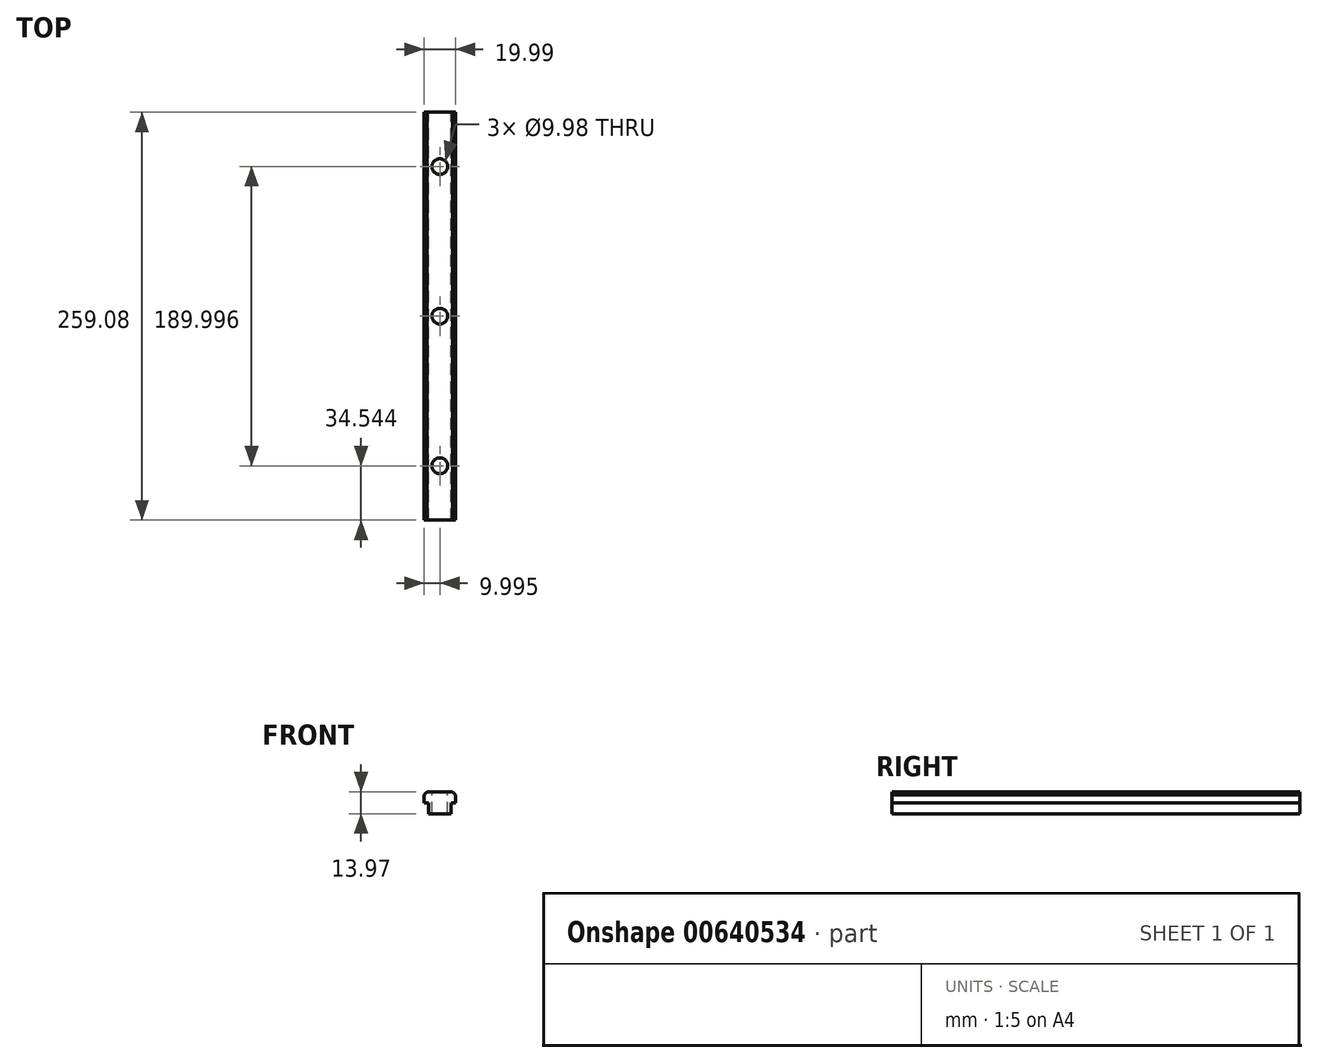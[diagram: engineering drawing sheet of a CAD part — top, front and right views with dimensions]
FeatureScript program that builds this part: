
annotation { "Feature Type Name" : "Feature", "Feature Type Description" : "" }
export const myFeature = defineFeature(function(context is Context, id is Id, definition is map)
    precondition{}
    {
        {
            var Q0;
            Q0=qCreatedBy(makeId("Front.planeOp"),FACE);
            var sketch = newSketch(context, id + "F0", { "sketchPlane" : qUnion([Q0])});
            skLineSegment(sketch, "E0", {"start": v(-13.06, -7) * mm, "end": v(0.93, -7) * mm});
            skLineSegment(sketch, "E1", {"start": v(0.93, -7) * mm, "end": v(0.93, 0) * mm});
            skLineSegment(sketch, "E2", {"start": v(0.93, 0) * mm, "end": v(3.93, 0) * mm});
            skLineSegment(sketch, "E3", {"start": v(3.93, 0) * mm, "end": v(3.93, 5) * mm});
            skLineSegment(sketch, "E4", {"start": v(-16.06, 5) * mm, "end": v(-16.06, 0) * mm});
            skLineSegment(sketch, "E5", {"start": v(-13.06, -7) * mm, "end": v(-13.06, 0) * mm});
            skLineSegment(sketch, "E6", {"start": v(-16.06, 0) * mm, "end": v(-13.06, 0) * mm});
            skLineSegment(sketch, "E7", {"start": v(-16.06, 5) * mm, "end": v(-14.06, 6.97) * mm});
            skLineSegment(sketch, "E8", {"start": v(-14.06, 6.97) * mm, "end": v(1.93, 6.97) * mm});
            skLineSegment(sketch, "E9", {"start": v(1.93, 6.97) * mm, "end": v(3.93, 5) * mm});
            skSolve(sketch);
        }
        {
            var Q0;
            Q0 = qSketchRegion(id + "F0", true);
            extrude(context, id + "F1", {"entities" : qUnion([Q0]), "depth" : 259.08 * mm, "offsetDistance" : 25.4 * mm});
        }
        {
            var Q0;
            Q0=makeQuery(id+"F1.opExtrude","SWEPT_FACE",FACE,{"disambiguationData":[OSD([sQuery(id+"F0.wireOp",EDGE,"E8")])]});
            var sketch = newSketch(context, id + "F2", { "sketchPlane" : qUnion([Q0])});
            skLineSegment(sketch, "E10", {"start": v(-65.38, -129.54) * mm, "end": v(65.39, -129.54) * mm});
            skLineSegment(sketch, "E11", {"start": v(-6.06, 0) * mm, "end": v(-6.06, -259.08) * mm});
            skCircle(sketch, "E12", {"center": v(-6.06, -129.54) * mm, "radius": 5 * mm});
            skCircle(sketch, "E13", {"center": v(-6.06, -34.54) * mm, "radius": 5 * mm});
            skCircle(sketch, "E14", {"center": v(-6.06, -224.54) * mm, "radius": 5 * mm});
            skSolve(sketch);
        }
        {
            var Q0;
            Q0 = qSketchRegion(id + "F2", true);
            extrude(context, id + "F3", {"entities" : qUnion([Q0]), "operationType" : NewBodyOperationType.REMOVE, "endBound" : BoundingType.THROUGH_ALL, "oppositeDirection" : true, "depth" : 25.4 * mm, "offsetDistance" : 25.4 * mm});
        }
    });
